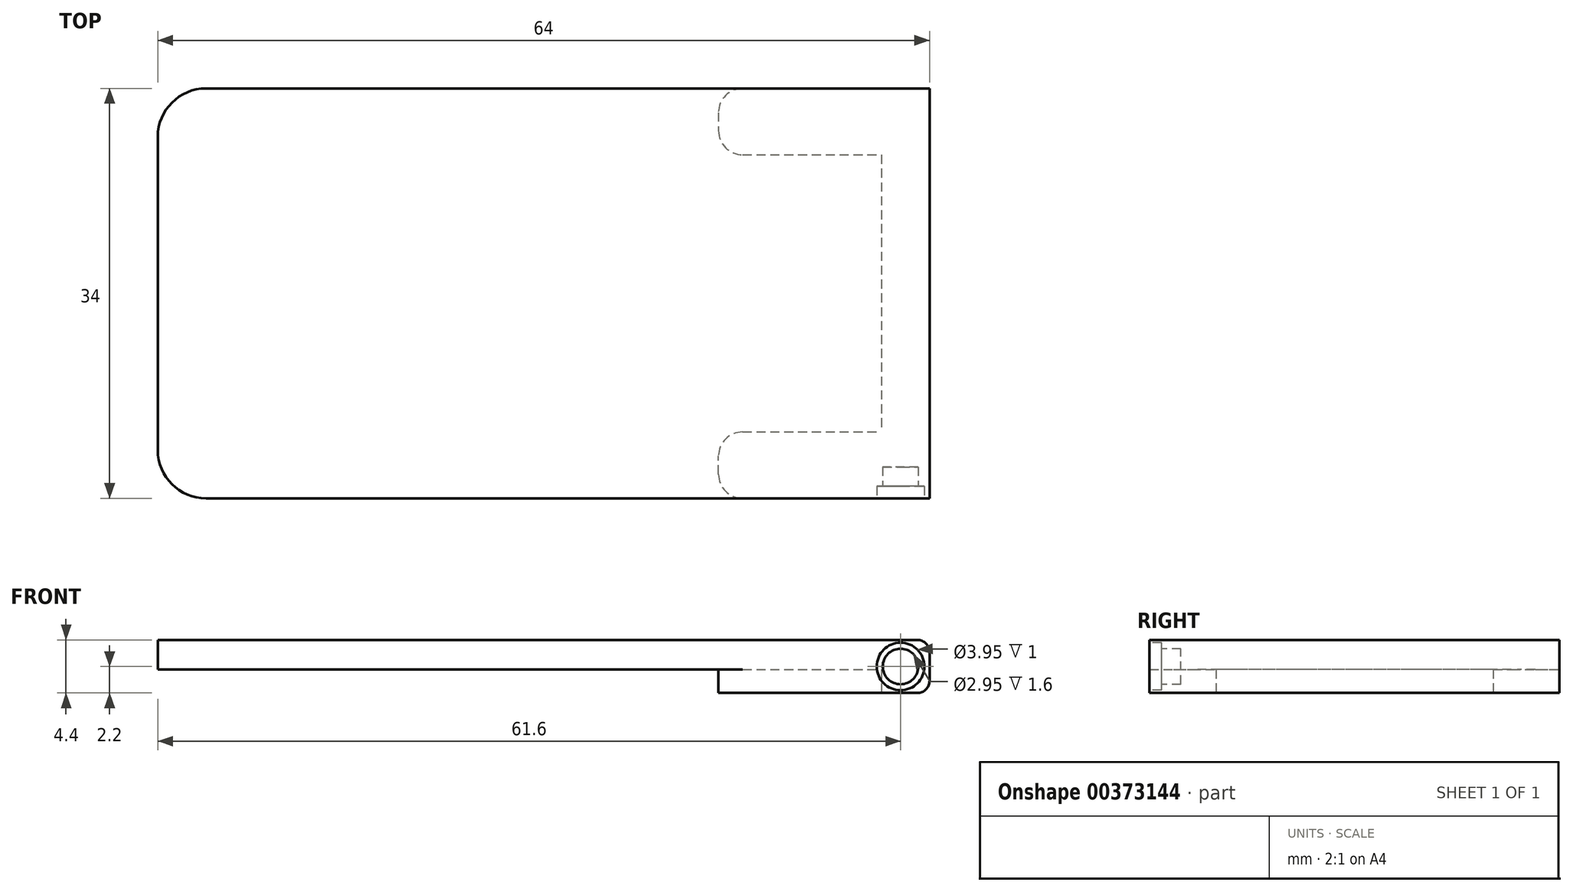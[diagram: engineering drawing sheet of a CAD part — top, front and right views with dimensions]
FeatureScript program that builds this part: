
annotation { "Feature Type Name" : "Feature", "Feature Type Description" : "" }
export const myFeature = defineFeature(function(context is Context, id is Id, definition is map)
    precondition{}
    {
        {
            var Q0;
            Q0=qCreatedBy(makeId("Top.planeOp"),FACE);
            var sketch = newSketch(context, id + "F0", { "sketchPlane" : qUnion([Q0])});
            skLineSegment(sketch, "E0.bottom", {"start": v(0, 0) * mm, "end": v(-60, 0) * mm});
            skLineSegment(sketch, "E0.top", {"start": v(0, 34) * mm, "end": v(-60, 34) * mm});
            skLineSegment(sketch, "E0.left", {"start": v(0, 0) * mm, "end": v(0, 34) * mm});
            skLineSegment(sketch, "E0.right", {"start": v(-64, 4) * mm, "end": v(-64, 30) * mm});
            skPoint(sketch, "E1.visualSharp", {"position": v(-64, 34) * mm});
            skArc(sketch, "E1.filletArc", {"start": v(-60, 34) * mm, "mid": v(-62.83, 32.83) * mm, "end": v(-64, 30) * mm});
            skPoint(sketch, "E2.visualSharp", {"position": v(-64, 0) * mm});
            skArc(sketch, "E2.filletArc", {"start": v(-64, 4) * mm, "mid": v(-62.83, 1.17) * mm, "end": v(-60, 0) * mm});
            skSolve(sketch);
        }
        {
            var Q0;
            Q0=makeQuery(id+"F0.imprint","IMPRINT",FACE,{"disambiguationData":[TD([[makeQuery(id+"F0.imprint","IMPRINT",EDGE,{"derivedFrom":sQuery(id+"F0.wireOp",EDGE,"E0.bottom")}),-1.0]])]});
            extrude(context, id + "F1", {"entities" : qUnion([Q0]), "depth" : 4.4 * mm});
        }
        {
            var Q0;
            Q0=makeQuery(id+"F1.opExtrude","CAP_FACE",FACE,{"disambiguationData":[OSD([sQuery(id+"F0.wireOp",EDGE,"E0.bottom"),sQuery(id+"F0.wireOp",EDGE,"E0.top"),sQuery(id+"F0.wireOp",EDGE,"E0.left"),sQuery(id+"F0.wireOp",EDGE,"E0.right"),sQuery(id+"F0.wireOp",EDGE,"E1.filletArc"),sQuery(id+"F0.wireOp",EDGE,"E2.filletArc")])],"isStart":true});
            var sketch = newSketch(context, id + "F2", { "sketchPlane" : qUnion([Q0])});
            skLineSegment(sketch, "E3.bottom", {"start": v(0, -5.5) * mm, "end": v(-4, -5.5) * mm, "construction": true});
            skLineSegment(sketch, "E3.top", {"start": v(0, -28.5) * mm, "end": v(-4, -28.5) * mm, "construction": true});
            skLineSegment(sketch, "E3.left", {"start": v(0, -5.5) * mm, "end": v(0, -28.5) * mm, "construction": true});
            skLineSegment(sketch, "E3.right", {"start": v(-4, -5.5) * mm, "end": v(-4, -28.5) * mm, "construction": true});
            skLineSegment(sketch, "E4.bottom", {"start": v(0, -34) * mm, "end": v(-15.5, -34) * mm, "construction": true});
            skLineSegment(sketch, "E4.top", {"start": v(0, -28.5) * mm, "end": v(-15.5, -28.5) * mm, "construction": true});
            skLineSegment(sketch, "E4.left", {"start": v(0, -34) * mm, "end": v(0, -28.5) * mm, "construction": true});
            skLineSegment(sketch, "E4.right", {"start": v(-17.5, -32) * mm, "end": v(-17.5, -30.5) * mm});
            skLineSegment(sketch, "E5.bottom", {"start": v(0, 0) * mm, "end": v(-15.5, 0) * mm, "construction": true});
            skLineSegment(sketch, "E5.top", {"start": v(0, -5.5) * mm, "end": v(-15.5, -5.5) * mm, "construction": true});
            skLineSegment(sketch, "E5.left", {"start": v(0, 0) * mm, "end": v(0, -5.5) * mm, "construction": true});
            skLineSegment(sketch, "E5.right", {"start": v(-17.5, -2) * mm, "end": v(-17.5, -3.5) * mm});
            skPoint(sketch, "E6.visualSharp", {"position": v(-17.5, -5.5) * mm});
            skArc(sketch, "E6.filletArc", {"start": v(-17.5, -3.5) * mm, "mid": v(-16.91, -4.91) * mm, "end": v(-15.5, -5.5) * mm});
            skPoint(sketch, "E7.visualSharp", {"position": v(-17.5, -28.5) * mm});
            skArc(sketch, "E7.filletArc", {"start": v(-15.5, -28.5) * mm, "mid": v(-16.91, -29.09) * mm, "end": v(-17.5, -30.5) * mm});
            skPoint(sketch, "E8.visualSharp", {"position": v(-17.5, -34) * mm});
            skArc(sketch, "E8.filletArc", {"start": v(-17.5, -32) * mm, "mid": v(-16.91, -33.41) * mm, "end": v(-15.5, -34) * mm});
            skPoint(sketch, "E9.visualSharp", {"position": v(-17.5, 0) * mm});
            skArc(sketch, "E9.filletArc", {"start": v(-15.5, 0) * mm, "mid": v(-16.91, -0.59) * mm, "end": v(-17.5, -2) * mm});
            skLineSegment(sketch, "E10", {"start": v(-15.5, -34) * mm, "end": v(-64, -34) * mm});
            skLineSegment(sketch, "E11", {"start": v(-64, -34) * mm, "end": v(-64, 0) * mm});
            skLineSegment(sketch, "E12", {"start": v(-64, 0) * mm, "end": v(-15.5, 0) * mm});
            skLineSegment(sketch, "E13", {"start": v(-15.5, -5.5) * mm, "end": v(-4, -5.5) * mm});
            skLineSegment(sketch, "E14", {"start": v(-4, -28.5) * mm, "end": v(-4, -5.5) * mm});
            skLineSegment(sketch, "E15", {"start": v(-15.5, -28.5) * mm, "end": v(-4, -28.5) * mm});
            skSolve(sketch);
        }
        {
            var Q0;
            Q0 = qSketchRegion(id + "F2", true);
            extrude(context, id + "F3", {"entities" : qUnion([Q0]), "operationType" : NewBodyOperationType.REMOVE, "oppositeDirection" : true, "depth" : 1.95 * mm});
        }
        {
            var Q0;
            Q0=makeQuery(id+"F1.opExtrude","CAP_FACE",FACE,{"disambiguationData":[OSD([sQuery(id+"F0.wireOp",EDGE,"E0.bottom"),sQuery(id+"F0.wireOp",EDGE,"E0.top"),sQuery(id+"F0.wireOp",EDGE,"E0.left"),sQuery(id+"F0.wireOp",EDGE,"E0.right"),sQuery(id+"F0.wireOp",EDGE,"E1.filletArc"),sQuery(id+"F0.wireOp",EDGE,"E2.filletArc")])],"isStart":false});
            var sketch = newSketch(context, id + "F4", { "sketchPlane" : qUnion([Q0])});
            skLineSegment(sketch, "E16", {"start": v(0, 17) * mm, "end": v(-13.55, 17) * mm, "construction": true});
            skPoint(sketch, "E16.endSnap0", {"position": v(0, 17) * mm});
            skSolve(sketch);
        }
        {
            var Q0;
            Q0=makeQuery(id+"F1.opExtrude","SWEPT_FACE",FACE,{"disambiguationData":[OSD([sQuery(id+"F0.wireOp",EDGE,"E0.left")])]});
            var sketch = newSketch(context, id + "F5", { "sketchPlane" : qUnion([Q0])});
            skLineSegment(sketch, "E17", {"start": v(17, 4.4) * mm, "end": v(17, 0) * mm, "construction": true});
            skSolve(sketch);
        }
        {
            var Q0;
            Q0=makeQuery(id+"F1.opExtrude","SWEPT_FACE",FACE,{"disambiguationData":[OSD([sQuery(id+"F0.wireOp",EDGE,"E0.bottom")])]});
            var sketch = newSketch(context, id + "F6", { "sketchPlane" : qUnion([Q0])});
            skCircle(sketch, "E18", {"center": v(-2.4, 2.2) * mm, "radius": 1.98 * mm});
            skPoint(sketch, "E18.centerSnap0", {"position": v(0, 2.2) * mm});
            skCircle(sketch, "E19", {"center": v(-2.4, 2.2) * mm, "radius": 1.48 * mm});
            skSolve(sketch);
        }
        {
            var Q0;
            Q0=sQuery(id+"F4.wireOp",EDGE,"E16");
            var Q1;
            Q1=sQuery(id+"F5.wireOp",EDGE,"E17");
            cPlane(context, id + "F7", {"entities" : qUnion([Q0, Q1]), "cplaneType" : CPlaneType.LINE_ANGLE, "offset" : 25 * mm, "angle" : 0 * degree, "width" : 150 * mm, "height" : 150 * mm});
        }
        {
            var Q0;
            Q0=makeQuery(id+"F6.imprint","IMPRINT",FACE,{"disambiguationData":[TD([[makeQuery(id+"F6.imprint","IMPRINT",EDGE,{"derivedFrom":sQuery(id+"F6.wireOp",EDGE,"E19")}),1.0]])]});
            extrude(context, id + "F8", {"entities" : qUnion([Q0]), "operationType" : NewBodyOperationType.REMOVE, "oppositeDirection" : true, "depth" : 2.6 * mm});
        }
        {
            var Q0;
            Q0 = qSketchRegion(id + "F6", true);
            extrude(context, id + "F9", {"entities" : qUnion([Q0]), "operationType" : NewBodyOperationType.REMOVE, "oppositeDirection" : true, "depth" : 1 * mm});
        }
        {
            var Q0;
            Q0=makeQuery(id+"F1.opExtrude","CAP_EDGE",EDGE,{"disambiguationData":[OSD([sQuery(id+"F0.wireOp",EDGE,"E0.left")])],"isStart":false});
            var Q1;
            Q1=makeQuery(id+"F1.opExtrude","CAP_EDGE",EDGE,{"disambiguationData":[OSD([sQuery(id+"F0.wireOp",EDGE,"E0.left")])],"isStart":true});
            fillet(context, id + "F10", {"entities" : qUnion([Q0, Q1]), "radius" : 1 * mm, "tangentPropagation" : true, "allowEdgeOverflow" : false});
        }
    });
